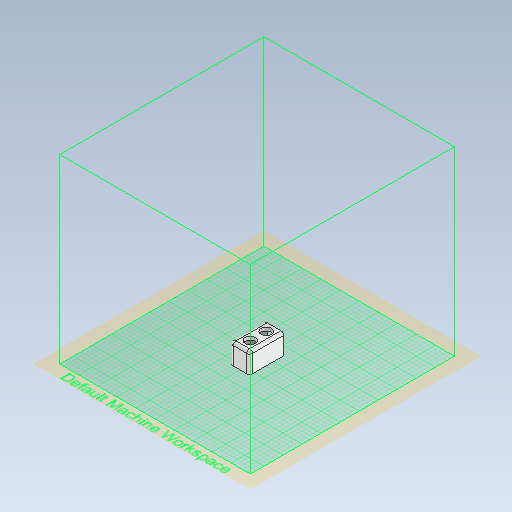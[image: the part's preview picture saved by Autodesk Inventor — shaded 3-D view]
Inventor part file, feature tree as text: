
AUTODESK INVENTOR PART (.ipt)
format: ipt  version: 2021 (Build 250183000, 183)  size: 1,425,408 bytes
history: native  units: in
note: dims shown in document units (in); Inventor stores cm internally (conversion verified against a paired STEP export)
features: extrude x7, other x7, fillet x4, sketch x1
ambient origin geometry x8: Origin, YZ Plane, XZ Plane, XY Plane, X Axis, Y Axis, Z Axis, Center Point
bodies: Body1 (feature_tree)
feature tree (19):
  extrude  "Base"  Depth=1.6535in
  extrude  "Top"  Depth=1.7717in TaperAngle=0.0deg
  extrude  "Walls"  Depth=1.122in
  fillet  "Outer"  Radius=1.122in
  extrude  "Wire"  Depth=1.122in
  fillet  "Inner Vertical"  Radius=1.122in
  extrude  "Half"  Depth=1.378in
  extrude  "Wall Holes"  Depth=1.378in
  fillet  "Wall Holes Fillet"  Radius=1.378in
  extrude  "Text"  Depth=0.7087in TaperAngle=0.0deg
  fillet  "Fillet6"  Radius=0.2362in
  sketch  "Sketch16"  dims[d6=5.9055in d7=1.6535in d8=1.7717in d9=0.0in d10=1.122in d11=1.122in d12=1.122in d13=1.122in d14=1.378in d15=1.378in d16=1.378in d19=0.7087in d20=0.0in d21=0.2362in d22=0.2362in d23=0.2362in d24=0.2362in d25=1.4764in d26=0.0in d27=0.8976in d28=0.8976in d29=0.8976in d30=0.8976in d31=0.689in d32=2.9528in d33=1.1811in d35=0.8858in d36=0.2362in d38=0.3937in d39=0.0in d41=0.1969in d44=2.9528in d45=0.0in d50=0.1181in d52=0.315in d53=0.0in d54=0.315in d55=0.1969in d56=0.0in d58=0.2559in d60=0.0197in d65=0.1575in d66=0.0787in d67=0.0787in d68=0.1575in d69=0.2774in d70=0.2774in d71=0.0499in d72=0.0499in d73=0.0787in d74=0.0in d75=0.0394in d46=0.0197in d47=0.0344in d48=0.0197in d49=0.0344in d59=0.0197in d61=0.0197in d62=0.0344in]
  other  "Base Sketch"
  other  "Top Sketch"
  other  "Walls Sketch"
  other  "Wire Sketch"
  other  "Half Sketch"
  other  "Wall Holes Sketch"
  other  "Text Sketch"
